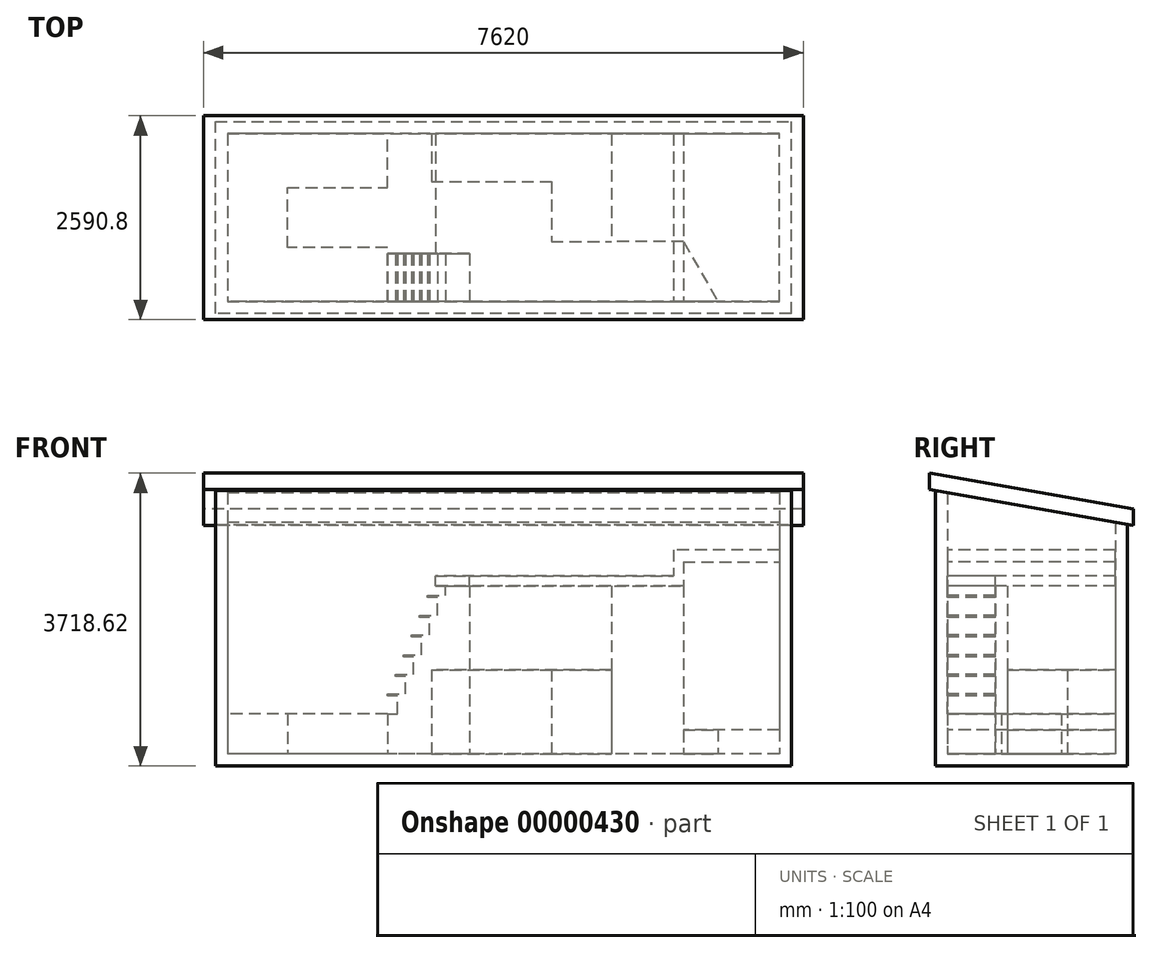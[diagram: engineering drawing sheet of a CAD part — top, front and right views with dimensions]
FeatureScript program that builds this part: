
annotation { "Feature Type Name" : "Feature", "Feature Type Description" : "" }
export const myFeature = defineFeature(function(context is Context, id is Id, definition is map)
    precondition{}
    {
        {
            var Q0;
            Q0=qCreatedBy(makeId("Top.planeOp"),FACE);
            var sketch = newSketch(context, id + "F0", { "sketchPlane" : qUnion([Q0])});
            skLineSegment(sketch, "E0.rect.bottom", {"start": v(3657.6, 1219.2) * mm, "end": v(-3657.6, 1219.2) * mm});
            skLineSegment(sketch, "E0.rect.top", {"start": v(3657.6, -1219.2) * mm, "end": v(-3657.6, -1219.2) * mm});
            skLineSegment(sketch, "E0.rect.left", {"start": v(3657.6, 1219.2) * mm, "end": v(3657.6, -1219.2) * mm});
            skLineSegment(sketch, "E0.rect.right", {"start": v(-3657.6, 1219.2) * mm, "end": v(-3657.6, -1219.2) * mm});
            skPoint(sketch, "E0.rect.middle", {"position": v(0, 0) * mm});
            skSolve(sketch);
        }
        {
            var Q0;
            Q0=makeQuery(id+"F0.imprint","IMPRINT",FACE,{"disambiguationData":[TD([[makeQuery(id+"F0.imprint","IMPRINT",EDGE,{"derivedFrom":sQuery(id+"F0.wireOp",EDGE,"E0.rect.bottom")}),1.0]])]});
            extrude(context, id + "F1", {"entities" : qUnion([Q0]), "depth" : 3498.85 * mm});
        }
        {
            var Q0;
            Q0=makeQuery(id+"F1.opExtrude","CAP_FACE",FACE,{"disambiguationData":[OSD([sQuery(id+"F0.wireOp",EDGE,"E0.rect.bottom"),sQuery(id+"F0.wireOp",EDGE,"E0.rect.top"),sQuery(id+"F0.wireOp",EDGE,"E0.rect.left"),sQuery(id+"F0.wireOp",EDGE,"E0.rect.right")])],"isStart":false});
            shell(context, id + "F2", {"entities" : qUnion([Q0]), "thickness" : 152.4 * mm});
        }
        {
            var Q0;
            Q0=makeQuery(id+"F1.opExtrude","SWEPT_FACE",FACE,{"disambiguationData":[OSD([sQuery(id+"F0.wireOp",EDGE,"E0.rect.left")])]});
            var sketch = newSketch(context, id + "F3", { "sketchPlane" : qUnion([Q0])});
            skLineSegment(sketch, "E1", {"start": v(-1219.2, 3498.85) * mm, "end": v(1219.2, 3068.9) * mm});
            skLineSegment(sketch, "E2", {"start": v(1219.2, 3068.9) * mm, "end": v(1219.2, 3498.85) * mm});
            skLineSegment(sketch, "E3", {"start": v(1219.2, 3498.85) * mm, "end": v(-1219.2, 3498.85) * mm});
            skSolve(sketch);
        }
        {
            var Q0;
            Q0=makeQuery(id+"F3.imprint","IMPRINT",FACE,{"disambiguationData":[TD([[makeQuery(id+"F3.imprint","IMPRINT",EDGE,{"derivedFrom":sQuery(id+"F3.wireOp",EDGE,"E1")}),1.0]])]});
            extrude(context, id + "F4", {"entities" : qUnion([Q0]), "operationType" : NewBodyOperationType.REMOVE, "endBound" : BoundingType.THROUGH_ALL, "oppositeDirection" : true, "depth" : 25.4 * mm});
        }
        {
            var Q0;
            Q0=qCreatedBy(makeId("Right.planeOp"),FACE);
            var sketch = newSketch(context, id + "F5", { "sketchPlane" : qUnion([Q0])});
            skLineSegment(sketch, "E4", {"start": v(-1295.4, 3512.29) * mm, "end": v(1295.4, 3055.46) * mm});
            skLineSegment(sketch, "E5", {"start": v(-1295.4, 3512.29) * mm, "end": v(-1295.4, 3718.62) * mm});
            skLineSegment(sketch, "E6", {"start": v(1295.4, 3261.8) * mm, "end": v(-1295.4, 3718.62) * mm});
            skLineSegment(sketch, "E7", {"start": v(1295.4, 3261.8) * mm, "end": v(1295.4, 3055.46) * mm});
            skPoint(sketch, "E8", {"position": v(0, 3283.87) * mm});
            skSolve(sketch);
        }
        {
            var Q0;
            Q0=makeQuery(id+"F5.imprint","IMPRINT",FACE,{"disambiguationData":[TD([[makeQuery(id+"F5.imprint","IMPRINT",EDGE,{"derivedFrom":sQuery(id+"F5.wireOp",EDGE,"E4")}),1.0]])]});
            extrude(context, id + "F6", {"entities" : qUnion([Q0]), "endBound" : BoundingType.SYMMETRIC, "depth" : 7620 * mm});
        }
        {
            var Q0;
            Q0=makeQuery(id+"F2.opShell","OFFSET_FACE",FACE,{"disambiguationData":[OSD([sQuery(id+"F0.wireOp",EDGE,"E0.rect.bottom"),sQuery(id+"F0.wireOp",EDGE,"E0.rect.top"),sQuery(id+"F0.wireOp",EDGE,"E0.rect.left"),sQuery(id+"F0.wireOp",EDGE,"E0.rect.right")])]});
            var sketch = newSketch(context, id + "F7", { "sketchPlane" : qUnion([Q0])});
            skLineSegment(sketch, "E9", {"start": v(-3505.2, 1066.8) * mm, "end": v(-3505.2, -1066.8) * mm});
            skLineSegment(sketch, "E10", {"start": v(-3505.2, -1066.8) * mm, "end": v(-1473.2, -1066.8) * mm});
            skLineSegment(sketch, "E11", {"start": v(-1473.2, -1066.8) * mm, "end": v(-1473.2, -381) * mm});
            skLineSegment(sketch, "E12", {"start": v(-1473.2, -381) * mm, "end": v(-2743.2, -381) * mm});
            skLineSegment(sketch, "E13", {"start": v(-2743.2, -381) * mm, "end": v(-2743.2, 381) * mm});
            skLineSegment(sketch, "E14", {"start": v(-2743.2, 381) * mm, "end": v(-1473.2, 381) * mm});
            skLineSegment(sketch, "E15", {"start": v(-1473.2, 381) * mm, "end": v(-1473.2, 1066.8) * mm});
            skLineSegment(sketch, "E16", {"start": v(-1473.2, 1066.8) * mm, "end": v(-3505.2, 1066.8) * mm});
            skLineSegment(sketch, "E17", {"start": v(3505.2, 1066.8) * mm, "end": v(-914.4, 1066.8) * mm});
            skLineSegment(sketch, "E18", {"start": v(1371.6, -304.8) * mm, "end": v(2286, -304.8) * mm});
            skLineSegment(sketch, "E19", {"start": v(2286, -304.8) * mm, "end": v(2725.94, -1066.8) * mm});
            skLineSegment(sketch, "E20", {"start": v(2725.94, -1066.8) * mm, "end": v(3505.2, -1066.8) * mm});
            skLineSegment(sketch, "E21", {"start": v(3505.2, -1066.8) * mm, "end": v(3505.2, 1066.8) * mm});
            skLineSegment(sketch, "E22", {"start": v(2286, -304.8) * mm, "end": v(2286, 1066.8) * mm});
            skLineSegment(sketch, "E23", {"start": v(1371.6, -304.8) * mm, "end": v(1371.6, 1066.8) * mm});
            skLineSegment(sketch, "E24", {"start": v(-914.4, 1066.8) * mm, "end": v(-914.4, 457.2) * mm});
            skLineSegment(sketch, "E25", {"start": v(-914.4, 457.2) * mm, "end": v(609.6, 457.2) * mm});
            skLineSegment(sketch, "E26", {"start": v(609.6, 457.2) * mm, "end": v(609.6, -304.8) * mm});
            skLineSegment(sketch, "E27", {"start": v(609.6, -304.8) * mm, "end": v(1371.6, -304.8) * mm});
            skSolve(sketch);
        }
        {
            var Q0;
            Q0=makeQuery(id+"F7.imprint","IMPRINT",FACE,{"disambiguationData":[TD([[makeQuery(id+"F7.imprint","IMPRINT",EDGE,{"derivedFrom":sQuery(id+"F7.wireOp",EDGE,"E9")}),1.0]])]});
            extrude(context, id + "F8", {"entities" : qUnion([Q0]), "depth" : 508 * mm});
        }
        {
            var Q0;
            Q0=makeQuery(id+"F8.opExtrude","CAP_FACE",FACE,{"disambiguationData":[OSD([sQuery(id+"F7.wireOp",EDGE,"E9"),sQuery(id+"F7.wireOp",EDGE,"E10"),sQuery(id+"F7.wireOp",EDGE,"E11"),sQuery(id+"F7.wireOp",EDGE,"E12"),sQuery(id+"F7.wireOp",EDGE,"E13"),sQuery(id+"F7.wireOp",EDGE,"E14"),sQuery(id+"F7.wireOp",EDGE,"E15"),sQuery(id+"F7.wireOp",EDGE,"E16")])],"isStart":false});
            var sketch = newSketch(context, id + "F9", { "sketchPlane" : qUnion([Q0])});
            skLineSegment(sketch, "E28.bottom", {"start": v(-2743.2, -381) * mm, "end": v(-1473.2, -381) * mm});
            skLineSegment(sketch, "E28.top", {"start": v(-2743.2, 381) * mm, "end": v(-1473.2, 381) * mm});
            skLineSegment(sketch, "E28.left", {"start": v(-2743.2, -381) * mm, "end": v(-2743.2, 381) * mm});
            skLineSegment(sketch, "E28.right", {"start": v(-1473.2, -381) * mm, "end": v(-1473.2, 381) * mm});
            skSolve(sketch);
        }
        {
            var Q0;
            Q0=makeQuery(id+"F7.imprint","IMPRINT",FACE,{"disambiguationData":[TD([[makeQuery(id+"F7.imprint","IMPRINT",EDGE,{"derivedFrom":sQuery(id+"F7.wireOp",EDGE,"E19")}),1.0]])]});
            extrude(context, id + "F10", {"entities" : qUnion([Q0]), "operationType" : NewBodyOperationType.ADD, "depth" : 304.8 * mm});
        }
        {
            var Q0;
            Q0=makeQuery(id+"F7.imprint","IMPRINT",FACE,{"disambiguationData":[TD([[sQuery(id+"F7.imprint",EDGE,"eb49c3ea-9785-4d08-b7cb-a81c8a1e7274"),1.0]])]});
            var Q1;
            {var subQ1=sQuery(id+"F7.wireOp",EDGE,"E23");Q1=makeQuery(id+"F7.imprint","IMPRINT",FACE,{"disambiguationData":[TD([[makeQuery(id+"F7.imprint","IMPRINT",EDGE,{"derivedFrom":subQ1}),1.0]])]});}
            extrude(context, id + "F11", {"entities" : qUnion([Q0, Q1]), "depth" : 1066.8 * mm});
        }
        {
            var Q0;
            Q0=makeQuery(id+"F2.opShell","OFFSET_FACE",FACE,{"disambiguationData":[OSD([sQuery(id+"F0.wireOp",EDGE,"E0.rect.top")])]});
            var sketch = newSketch(context, id + "F12", { "sketchPlane" : qUnion([Q0])});
            skLineSegment(sketch, "E29.bottom", {"start": v(863.6, 2413) * mm, "end": v(-2286, 2413) * mm});
            skLineSegment(sketch, "E29.top", {"start": v(863.6, 2286) * mm, "end": v(-2286, 2286) * mm});
            skLineSegment(sketch, "E29.left", {"start": v(863.6, 2413) * mm, "end": v(863.6, 2286) * mm});
            skLineSegment(sketch, "E29.right", {"start": v(-2286, 2413) * mm, "end": v(-2286, 2286) * mm});
            skLineSegment(sketch, "E30", {"start": v(1473.2, 152.4) * mm, "end": v(1473.2, 660.4) * mm});
            skLineSegment(sketch, "E31", {"start": v(-2286, 152.4) * mm, "end": v(-2286, 2286) * mm, "construction": true});
            skLineSegment(sketch, "E32", {"start": v(431.8, 2413) * mm, "end": v(431.8, 152.4) * mm});
            skLineSegment(sketch, "E33", {"start": v(1473.2, 660.4) * mm, "end": v(1346.2, 660.4) * mm});
            skLineSegment(sketch, "E34", {"start": v(1346.2, 660.4) * mm, "end": v(1346.2, 885.37) * mm});
            skLineSegment(sketch, "E35", {"start": v(1346.2, 885.37) * mm, "end": v(1473.2, 885.37) * mm});
            skLineSegment(sketch, "E36", {"start": v(1473.2, 885.37) * mm, "end": v(1473.2, 910.77) * mm});
            skLineSegment(sketch, "E37", {"start": v(1473.2, 910.77) * mm, "end": v(1244.6, 910.77) * mm});
            skLineSegment(sketch, "E38", {"start": v(1244.6, 910.77) * mm, "end": v(1244.6, 1135.74) * mm});
            skLineSegment(sketch, "E39", {"start": v(1244.6, 1135.74) * mm, "end": v(1371.6, 1135.74) * mm});
            skLineSegment(sketch, "E40", {"start": v(1371.6, 1135.74) * mm, "end": v(1371.6, 1161.14) * mm});
            skLineSegment(sketch, "E41", {"start": v(1371.6, 1161.14) * mm, "end": v(1143, 1161.14) * mm});
            skLineSegment(sketch, "E42", {"start": v(1143, 1161.14) * mm, "end": v(1143, 1386.11) * mm});
            skLineSegment(sketch, "E43", {"start": v(1143, 1386.11) * mm, "end": v(1270, 1386.11) * mm});
            skLineSegment(sketch, "E44", {"start": v(1270, 1386.11) * mm, "end": v(1270, 1411.51) * mm});
            skLineSegment(sketch, "E45", {"start": v(1270, 1411.51) * mm, "end": v(1041.4, 1411.51) * mm});
            skLineSegment(sketch, "E46", {"start": v(1041.4, 1411.51) * mm, "end": v(1041.4, 1636.49) * mm});
            skLineSegment(sketch, "E47", {"start": v(1041.4, 1636.49) * mm, "end": v(1168.4, 1636.49) * mm});
            skLineSegment(sketch, "E48", {"start": v(1168.4, 1636.49) * mm, "end": v(1168.4, 1661.89) * mm});
            skLineSegment(sketch, "E49", {"start": v(1168.4, 1661.89) * mm, "end": v(939.8, 1661.89) * mm});
            skLineSegment(sketch, "E50", {"start": v(939.8, 1661.89) * mm, "end": v(939.8, 1886.86) * mm});
            skLineSegment(sketch, "E51", {"start": v(939.8, 1886.86) * mm, "end": v(1066.8, 1886.86) * mm});
            skLineSegment(sketch, "E52", {"start": v(1066.8, 1886.86) * mm, "end": v(1066.8, 1912.26) * mm});
            skLineSegment(sketch, "E53", {"start": v(1066.8, 1912.26) * mm, "end": v(838.2, 1912.26) * mm});
            skLineSegment(sketch, "E54", {"start": v(838.2, 1912.26) * mm, "end": v(838.2, 2137.23) * mm});
            skLineSegment(sketch, "E55", {"start": v(838.2, 2137.23) * mm, "end": v(965.2, 2137.23) * mm});
            skLineSegment(sketch, "E56", {"start": v(965.2, 2137.23) * mm, "end": v(965.2, 2162.63) * mm});
            skLineSegment(sketch, "E57", {"start": v(965.2, 2162.63) * mm, "end": v(736.6, 2162.63) * mm});
            skLineSegment(sketch, "E58", {"start": v(736.6, 2162.63) * mm, "end": v(736.6, 2387.6) * mm});
            skLineSegment(sketch, "E59", {"start": v(736.6, 2387.6) * mm, "end": v(863.6, 2387.6) * mm});
            skLineSegment(sketch, "E60", {"start": v(863.6, 2387.6) * mm, "end": v(863.6, 2413) * mm});
            skLineSegment(sketch, "E61", {"start": v(863.6, 2413) * mm, "end": v(431.8, 2413) * mm});
            skLineSegment(sketch, "E62", {"start": v(-2286, 2413) * mm, "end": v(-2286, 2590.8) * mm});
            skLineSegment(sketch, "E63", {"start": v(-2286, 2590.8) * mm, "end": v(-3505.2, 2590.8) * mm});
            skLineSegment(sketch, "E64", {"start": v(-3505.2, 2590.8) * mm, "end": v(-3505.2, 2743.2) * mm});
            skLineSegment(sketch, "E65", {"start": v(-3505.2, 2743.2) * mm, "end": v(-2159, 2743.2) * mm});
            skLineSegment(sketch, "E66", {"start": v(-2159, 2743.2) * mm, "end": v(-2159, 2413) * mm});
            skSolve(sketch);
        }
        {
            var Q0;
            {var subQ4=sQuery(id+"F12.wireOp",EDGE,"E29.left");Q0=makeQuery(id+"F12.imprint","IMPRINT",FACE,{"disambiguationData":[TD([[makeQuery(id+"F12.imprint","IMPRINT",EDGE,{"derivedFrom":subQ4}),-1.0]])]});}
            var Q1;
            {var subQ5=sQuery(id+"F12.wireOp",EDGE,"E29.right");Q1=makeQuery(id+"F12.imprint","IMPRINT",FACE,{"disambiguationData":[TD([[makeQuery(id+"F12.imprint","IMPRINT",EDGE,{"derivedFrom":subQ5}),1.0]])]});}
            var Q2;
            {var subQ1=sQuery(id+"F12.wireOp",EDGE,"E59");Q2=makeQuery(id+"F12.imprint","IMPRINT",FACE,{"disambiguationData":[TD([[makeQuery(id+"F12.imprint","IMPRINT",EDGE,{"derivedFrom":subQ1}),1.0]])]});}
            var Q3;
            {var subQ1=sQuery(id+"F12.wireOp",EDGE,"E62");Q3=makeQuery(id+"F12.imprint","IMPRINT",FACE,{"disambiguationData":[TD([[makeQuery(id+"F12.imprint","IMPRINT",EDGE,{"derivedFrom":subQ1}),-1.0]])]});}
            var Q4;
            Q4=makeQuery(id+"F2.opShell","OFFSET_FACE",FACE,{"disambiguationData":[OSD([sQuery(id+"F0.wireOp",EDGE,"E0.rect.bottom")])]});
            extrude(context, id + "F13", {"entities" : qUnion([Q0, Q1, Q2, Q3]), "endBound" : BoundingType.UP_TO_SURFACE, "endBoundEntityFace" : qUnion([Q4]), "depth" : 25.4 * mm});
        }
        {
            var Q0;
            {var subQ4=sQuery(id+"F12.wireOp",EDGE,"E30");Q0=makeQuery(id+"F12.imprint","IMPRINT",FACE,{"disambiguationData":[TD([[makeQuery(id+"F12.imprint","IMPRINT",EDGE,{"derivedFrom":subQ4}),1.0]])]});}
            var Q1;
            {var subQ1=sQuery(id+"F12.wireOp",EDGE,"E59");Q1=makeQuery(id+"F12.imprint","IMPRINT",FACE,{"disambiguationData":[TD([[makeQuery(id+"F12.imprint","IMPRINT",EDGE,{"derivedFrom":subQ1}),1.0]])]});}
            extrude(context, id + "F14", {"entities" : qUnion([Q0, Q1]), "depth" : 609.6 * mm});
        }
        {
            var Q0;
            Q0=makeQuery(id+"F13.opExtrude","SWEPT_FACE",FACE,{"disambiguationData":[OSD([sQuery(id+"F12.wireOp",EDGE,"E29.bottom"),sQuery(id+"F12.wireOp",EDGE,"E61")])]});
            var sketch = newSketch(context, id + "F15", { "sketchPlane" : qUnion([Q0])});
            skLineSegment(sketch, "E67.bottom", {"start": v(-863.6, -457.2) * mm, "end": v(-431.8, -457.2) * mm});
            skLineSegment(sketch, "E67.top", {"start": v(-863.6, -1066.8) * mm, "end": v(-431.8, -1066.8) * mm});
            skLineSegment(sketch, "E67.left", {"start": v(-863.6, -457.2) * mm, "end": v(-863.6, -1066.8) * mm});
            skLineSegment(sketch, "E67.right", {"start": v(-431.8, -457.2) * mm, "end": v(-431.8, -1066.8) * mm});
            skSolve(sketch);
        }
        {
            var Q0;
            Q0=makeQuery(id+"F15.imprint","IMPRINT",FACE,{"disambiguationData":[TD([[makeQuery(id+"F15.imprint","IMPRINT",EDGE,{"derivedFrom":sQuery(id+"F15.wireOp",EDGE,"E67.bottom")}),-1.0]])]});
            extrude(context, id + "F16", {"entities" : qUnion([Q0]), "operationType" : NewBodyOperationType.REMOVE, "oppositeDirection" : true, "depth" : 127 * mm});
        }
        {
            var Q0;
            Q0=makeQuery(id+"F7.imprint","IMPRINT",FACE,{"disambiguationData":[TD([[makeQuery(id+"F7.imprint","IMPRINT",EDGE,{"derivedFrom":sQuery(id+"F7.wireOp",EDGE,"E18")}),1.0]])]});
            extrude(context, id + "F17", {"entities" : qUnion([Q0]), "endBound" : BoundingType.UP_TO_NEXT, "depth" : 25.4 * mm});
        }
        {
            var Q0;
            Q0=makeQuery(id+"F7.imprint","IMPRINT",FACE,{"disambiguationData":[TD([[makeQuery(id+"F7.imprint","IMPRINT",EDGE,{"derivedFrom":sQuery(id+"F7.wireOp",EDGE,"E19")}),1.0]])]});
            extrude(context, id + "F18", {"entities" : qUnion([Q0]), "depth" : 304.8 * mm});
        }
    });
